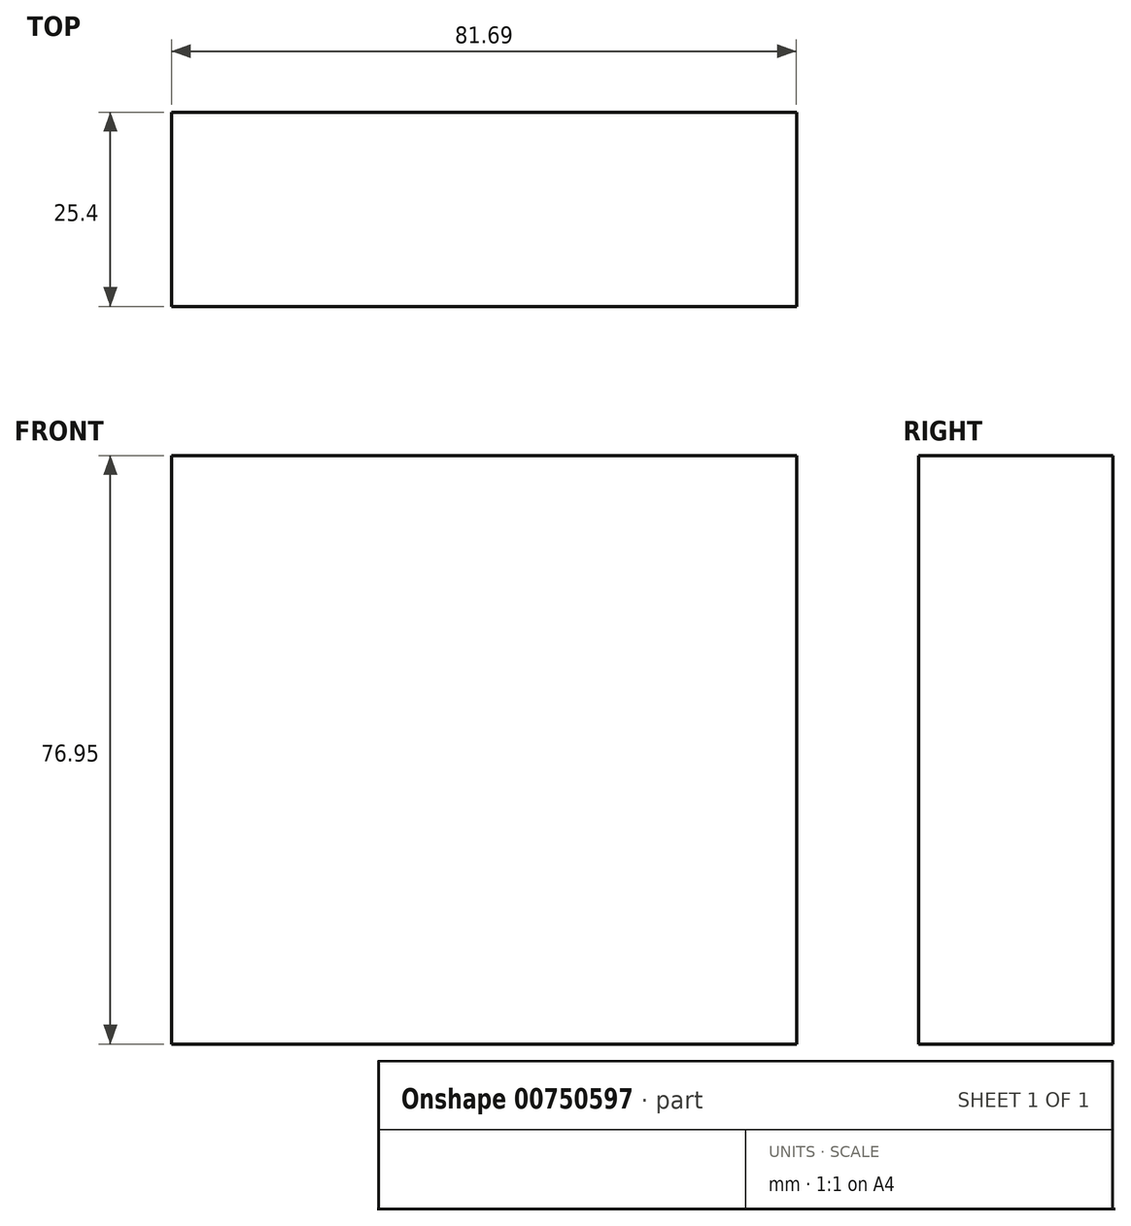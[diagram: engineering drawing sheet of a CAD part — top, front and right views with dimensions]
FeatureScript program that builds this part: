
annotation { "Feature Type Name" : "Feature", "Feature Type Description" : "" }
export const myFeature = defineFeature(function(context is Context, id is Id, definition is map)
    precondition{}
    {
        {
            var Q0;
            Q0=qCreatedBy(makeId("Front.planeOp"),FACE);
            var sketch = newSketch(context, id + "F0", { "sketchPlane" : qUnion([Q0])});
            skLineSegment(sketch, "E0.bottom", {"start": v(-45.8, -25.52) * mm, "end": v(35.9, -25.52) * mm});
            skLineSegment(sketch, "E0.top", {"start": v(-45.8, 51.43) * mm, "end": v(35.9, 51.43) * mm});
            skLineSegment(sketch, "E0.left", {"start": v(-45.8, -25.52) * mm, "end": v(-45.8, 51.43) * mm});
            skLineSegment(sketch, "E0.right", {"start": v(35.9, -25.52) * mm, "end": v(35.9, 51.43) * mm});
            skSolve(sketch);
        }
        {
            var Q0;
            Q0=makeQuery(id+"F0.imprint","IMPRINT",FACE,{"disambiguationData":[TD([[makeQuery(id+"F0.imprint","IMPRINT",EDGE,{"derivedFrom":sQuery(id+"F0.wireOp",EDGE,"E0.bottom")}),1.0]])]});
            extrude(context, id + "F1", {"entities" : qUnion([Q0]), "oppositeDirection" : true, "depth" : 25.4 * mm, "offsetDistance" : 25.4 * mm});
        }
    });
